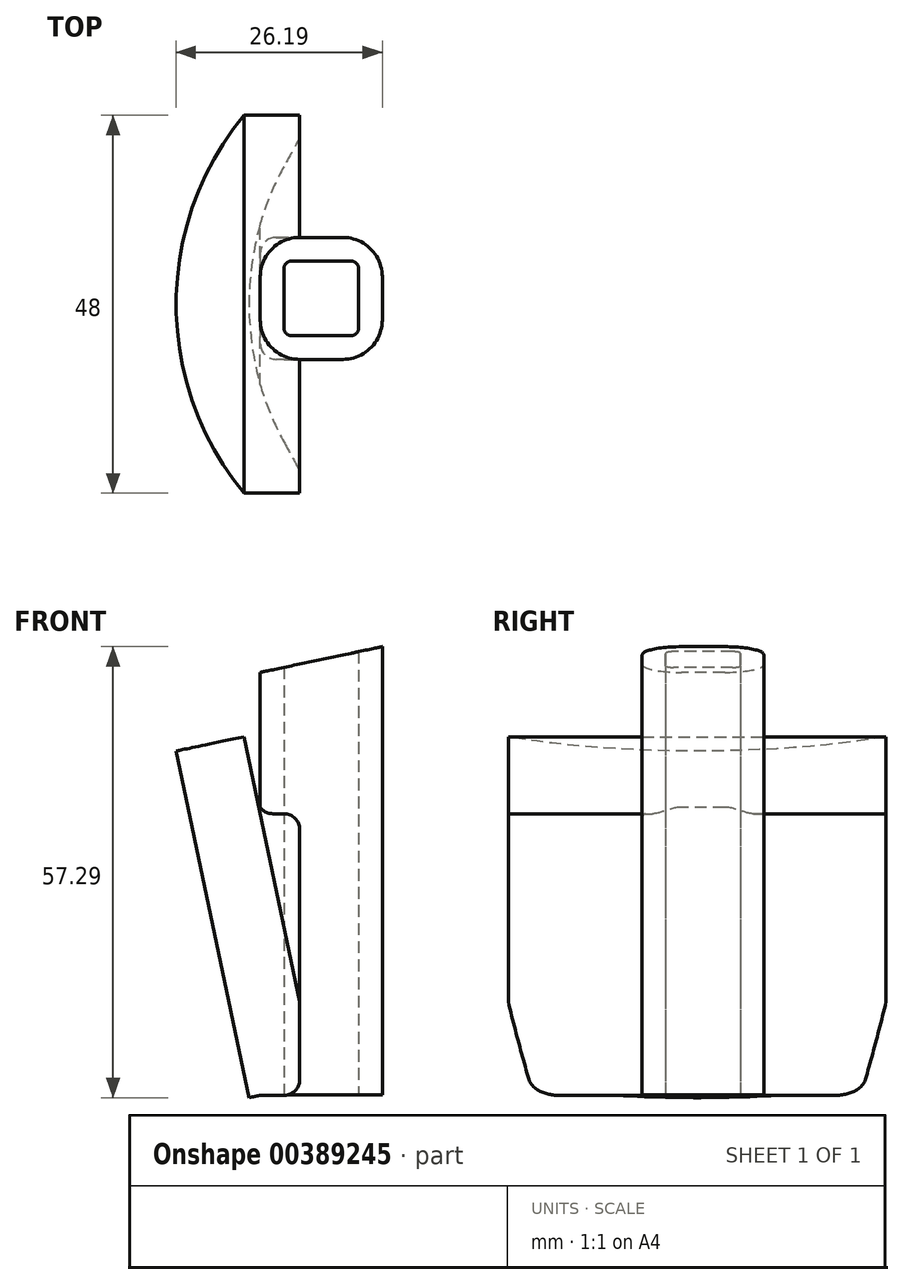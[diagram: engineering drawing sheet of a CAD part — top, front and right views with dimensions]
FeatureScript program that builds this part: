
annotation { "Feature Type Name" : "Feature", "Feature Type Description" : "" }
export const myFeature = defineFeature(function(context is Context, id is Id, definition is map)
    precondition{}
    {
        {
            var Q0;
            Q0=qCreatedBy(makeId("Top.planeOp"),FACE);
            var sketch = newSketch(context, id + "F0", { "sketchPlane" : qUnion([Q0])});
            skLineSegment(sketch, "E0.bottom", {"start": v(0, 0) * mm, "end": v(-9.5, 0) * mm});
            skLineSegment(sketch, "E0.top", {"start": v(0, 9.5) * mm, "end": v(-9.5, 9.5) * mm});
            skLineSegment(sketch, "E0.left", {"start": v(0, 0) * mm, "end": v(0, 9.5) * mm});
            skLineSegment(sketch, "E0.right", {"start": v(-9.5, 0) * mm, "end": v(-9.5, 9.5) * mm});
            skLineSegment(sketch, "E1.0", {"start": v(3, 12.5) * mm, "end": v(-12.5, 12.5) * mm});
            skLineSegment(sketch, "E1.1", {"start": v(3, -3) * mm, "end": v(3, 12.5) * mm});
            skLineSegment(sketch, "E1.2", {"start": v(3, -3) * mm, "end": v(-12.5, -3) * mm});
            skLineSegment(sketch, "E1.3", {"start": v(-12.5, -3) * mm, "end": v(-12.5, 12.5) * mm});
            skSolve(sketch);
        }
        {
            var Q0;
            Q0=makeQuery(id+"F0.imprint","IMPRINT",FACE,{"disambiguationData":[TD([[makeQuery(id+"F0.imprint","IMPRINT",EDGE,{"derivedFrom":sQuery(id+"F0.wireOp",EDGE,"E0.bottom")}),1.0]])]});
            extrude(context, id + "F1", {"entities" : qUnion([Q0]), "depth" : 100 * mm});
        }
        {
            var Q0;
            Q0=makeQuery(id+"F1.opExtrude","SWEPT_EDGE",EDGE,{"disambiguationData":[OSD([sQuery(id+"F0.wireOp",EDGE,"E1.2"),sQuery(id+"F0.wireOp",EDGE,"E1.3")])]});
            var Q1;
            Q1=makeQuery(id+"F1.opExtrude","SWEPT_EDGE",EDGE,{"disambiguationData":[OSD([sQuery(id+"F0.wireOp",EDGE,"E1.0"),sQuery(id+"F0.wireOp",EDGE,"E1.3")])]});
            var Q2;
            Q2=makeQuery(id+"F1.opExtrude","SWEPT_EDGE",EDGE,{"disambiguationData":[OSD([sQuery(id+"F0.wireOp",EDGE,"E1.0"),sQuery(id+"F0.wireOp",EDGE,"E1.1")])]});
            var Q3;
            Q3=makeQuery(id+"F1.opExtrude","SWEPT_EDGE",EDGE,{"disambiguationData":[OSD([sQuery(id+"F0.wireOp",EDGE,"E1.1"),sQuery(id+"F0.wireOp",EDGE,"E1.2")])]});
            fillet(context, id + "F2", {"entities" : qUnion([Q0, Q1, Q2, Q3]), "radius" : 5 * mm, "tangentPropagation" : true, "allowEdgeOverflow" : false});
        }
        {
            var Q0;
            Q0=makeQuery(id+"F1.opExtrude","SWEPT_EDGE",EDGE,{"disambiguationData":[OSD([sQuery(id+"F0.wireOp",EDGE,"E0.top"),sQuery(id+"F0.wireOp",EDGE,"E0.right")])]});
            var Q1;
            Q1=makeQuery(id+"F1.opExtrude","SWEPT_EDGE",EDGE,{"disambiguationData":[OSD([sQuery(id+"F0.wireOp",EDGE,"E0.top"),sQuery(id+"F0.wireOp",EDGE,"E0.left")])]});
            var Q2;
            Q2=makeQuery(id+"F1.opExtrude","SWEPT_EDGE",EDGE,{"disambiguationData":[OSD([sQuery(id+"F0.wireOp",EDGE,"E0.bottom"),sQuery(id+"F0.wireOp",EDGE,"E0.left")])]});
            var Q3;
            Q3=makeQuery(id+"F1.opExtrude","SWEPT_EDGE",EDGE,{"disambiguationData":[OSD([sQuery(id+"F0.wireOp",EDGE,"E0.bottom"),sQuery(id+"F0.wireOp",EDGE,"E0.right")])]});
            fillet(context, id + "F3", {"entities" : qUnion([Q0, Q1, Q2, Q3]), "radius" : 1 * mm, "tangentPropagation" : true, "allowEdgeOverflow" : false});
        }
        {
            var Q0;
            Q0=makeQuery(id+"F0.imprint","IMPRINT",FACE,{"disambiguationData":[TD([[makeQuery(id+"F0.imprint","IMPRINT",EDGE,{"derivedFrom":sQuery(id+"F0.wireOp",EDGE,"E0.bottom")}),-1.0]])]});
            var Q1;
            Q1=makeQuery(id+"F0.imprint","IMPRINT",FACE,{"disambiguationData":[TD([[makeQuery(id+"F0.imprint","IMPRINT",EDGE,{"derivedFrom":sQuery(id+"F0.wireOp",EDGE,"E0.bottom")}),1.0]])]});
            extrude(context, id + "F4", {"entities" : qUnion([Q0, Q1]), "operationType" : NewBodyOperationType.ADD, "depth" : 2 * mm});
        }
        {
            var Q0;
            Q0=makeQuery(id+"F4.opExtrude","SWEPT_EDGE",EDGE,{"disambiguationData":[OSD([sQuery(id+"F0.wireOp",EDGE,"E1.2"),sQuery(id+"F0.wireOp",EDGE,"E1.3")])]});
            var Q1;
            Q1=makeQuery(id+"F4.opExtrude","SWEPT_EDGE",EDGE,{"disambiguationData":[OSD([sQuery(id+"F0.wireOp",EDGE,"E1.1"),sQuery(id+"F0.wireOp",EDGE,"E1.2")])]});
            var Q2;
            Q2=makeQuery(id+"F4.opExtrude","SWEPT_EDGE",EDGE,{"disambiguationData":[OSD([sQuery(id+"F0.wireOp",EDGE,"E1.0"),sQuery(id+"F0.wireOp",EDGE,"E1.1")])]});
            var Q3;
            Q3=makeQuery(id+"F4.opExtrude","SWEPT_EDGE",EDGE,{"disambiguationData":[OSD([sQuery(id+"F0.wireOp",EDGE,"E1.0"),sQuery(id+"F0.wireOp",EDGE,"E1.3")])]});
            fillet(context, id + "F5", {"entities" : qUnion([Q0, Q1, Q2, Q3]), "radius" : 2 * mm, "tangentPropagation" : true, "allowEdgeOverflow" : false});
        }
        {
            var Q0;
            Q0=qCreatedBy(makeId("Front.planeOp"),FACE);
            var sketch = newSketch(context, id + "F6", { "sketchPlane" : qUnion([Q0])});
            skLineSegment(sketch, "E2", {"start": v(-23.85, 87.89) * mm, "end": v(23.32, 97.82) * mm});
            skLineSegment(sketch, "E3.0", {"start": v(-26.94, 102.56) * mm, "end": v(20.23, 112.5) * mm});
            skLineSegment(sketch, "E4", {"start": v(-26.94, 102.56) * mm, "end": v(-23.85, 87.89) * mm});
            skLineSegment(sketch, "E5", {"start": v(20.23, 112.5) * mm, "end": v(23.32, 97.82) * mm});
            skLineSegment(sketch, "E6", {"start": v(-13.99, 36.24) * mm, "end": v(-12.51, 36.55) * mm});
            skLineSegment(sketch, "E7.0", {"start": v(-21.2, 70.49) * mm, "end": v(-12.51, 72.32) * mm});
            skLineSegment(sketch, "E8", {"start": v(-21.2, 70.49) * mm, "end": v(-13.99, 36.24) * mm});
            skLineSegment(sketch, "E9", {"start": v(-12.51, 36.55) * mm, "end": v(-7.49, 36.55) * mm});
            skLineSegment(sketch, "E10", {"start": v(-7.49, 36.55) * mm, "end": v(-7.49, 72.32) * mm});
            skLineSegment(sketch, "E11", {"start": v(-7.49, 72.32) * mm, "end": v(-12.51, 72.32) * mm});
            skSolve(sketch);
        }
        {
            var Q0;
            Q0=makeQuery(id+"F6.imprint","IMPRINT",FACE,{"disambiguationData":[TD([[makeQuery(id+"F6.imprint","IMPRINT",EDGE,{"derivedFrom":sQuery(id+"F6.wireOp",EDGE,"E2")}),1.0]])]});
            extrude(context, id + "F7", {"entities" : qUnion([Q0]), "operationType" : NewBodyOperationType.REMOVE, "oppositeDirection" : true, "depth" : 25 * mm, "symmetric" : true});
        }
        {
            var Q0;
            Q0=makeQuery(id+"F6.imprint","IMPRINT",FACE,{"disambiguationData":[TD([[makeQuery(id+"F6.imprint","IMPRINT",EDGE,{"derivedFrom":sQuery(id+"F6.wireOp",EDGE,"E6")}),1.0]])]});
            extrude(context, id + "F8", {"entities" : qUnion([Q0]), "operationType" : NewBodyOperationType.ADD, "depth" : 20 * mm, "offsetDistance" : 25 * mm});
        }
        {
            var Q0;
            Q0=makeQuery(id+"F8.opExtrude","CAP_FACE",FACE,{"disambiguationData":[OSD([sQuery(id+"F6.wireOp",EDGE,"E6"),sQuery(id+"F6.wireOp",EDGE,"E7.0"),sQuery(id+"F6.wireOp",EDGE,"E8"),sQuery(id+"F6.wireOp",EDGE,"E9"),sQuery(id+"F6.wireOp",EDGE,"E10"),sQuery(id+"F6.wireOp",EDGE,"E11")])],"isStart":false});
            extrude(context, id + "F9", {"entities" : qUnion([Q0]), "operationType" : NewBodyOperationType.ADD, "oppositeDirection" : true, "depth" : 48 * mm, "offsetDistance" : 25 * mm});
        }
        {
            var Q0;
            {var subQ0=sQuery(id+"F0.wireOp",EDGE,"E1.3");var subQ1=sQuery(id+"F0.wireOp",EDGE,"E1.2");var subQ2=sQuery(id+"F0.wireOp",EDGE,"E1.1");var subQ3=sQuery(id+"F0.wireOp",EDGE,"E1.0");Q0=makeQuery(id+"F4.boolean.opBoolean","MERGE",FACE,{"derivedFrom":[makeQuery(id+"F1.opExtrude","CAP_FACE",FACE,{"disambiguationData":[OSD([sQuery(id+"F0.wireOp",EDGE,"E0.bottom"),sQuery(id+"F0.wireOp",EDGE,"E0.top"),sQuery(id+"F0.wireOp",EDGE,"E0.left"),sQuery(id+"F0.wireOp",EDGE,"E0.right"),subQ3,subQ2,subQ1,subQ0])],"isStart":true}),makeQuery(id+"F4.opExtrude","CAP_FACE",FACE,{"disambiguationData":[OSD([subQ3,subQ2,subQ1,subQ0])],"isStart":true})]});}
            extrude(context, id + "F10", {"entities" : qUnion([Q0]), "operationType" : NewBodyOperationType.REMOVE, "oppositeDirection" : true, "depth" : 36.6 * mm, "offsetDistance" : 25 * mm});
        }
        {
            var Q0;
            {var subQ0=sQuery(id+"F6.wireOp",EDGE,"E7.0");Q0=makeQuery(id+"F9.boolean.opBoolean","MERGE",FACE,{"derivedFrom":[makeQuery(id+"F8.opExtrude","SWEPT_FACE",FACE,{"disambiguationData":[OSD([subQ0])]}),makeQuery(id+"F9.opExtrude","SWEPT_FACE",FACE,{"disambiguationData":[OSD([subQ0])]})]});}
            var sketch = newSketch(context, id + "F11", { "sketchPlane" : qUnion([Q0])});
            skArc(sketch, "E12", {"start": v(2.65, 28) * mm, "mid": v(-6.15, 4) * mm, "end": v(2.65, -20) * mm});
            skLineSegment(sketch, "E13", {"start": v(2.65, -20) * mm, "end": v(-6.22, -20) * mm});
            skLineSegment(sketch, "E14", {"start": v(-6.22, -20) * mm, "end": v(-6.22, 28) * mm});
            skLineSegment(sketch, "E15", {"start": v(-6.22, 28) * mm, "end": v(2.65, 28) * mm});
            skSolve(sketch);
        }
        {
            var Q0;
            Q0=makeQuery(id+"F11.imprint","IMPRINT",FACE,{"disambiguationData":[TD([[makeQuery(id+"F11.imprint","IMPRINT",EDGE,{"derivedFrom":sQuery(id+"F11.wireOp",EDGE,"E12")}),-1.0]])]});
            extrude(context, id + "F12", {"entities" : qUnion([Q0]), "operationType" : NewBodyOperationType.REMOVE, "endBound" : BoundingType.THROUGH_ALL, "oppositeDirection" : true, "depth" : 25 * mm, "offsetDistance" : 25 * mm});
        }
        {
            var Q0;
            {var subQ0=sQuery(id+"F6.wireOp",EDGE,"E7.0");Q0=makeQuery(id+"F9.boolean.opBoolean","MERGE",FACE,{"derivedFrom":[makeQuery(id+"F8.opExtrude","SWEPT_FACE",FACE,{"disambiguationData":[OSD([subQ0])]}),makeQuery(id+"F9.opExtrude","SWEPT_FACE",FACE,{"disambiguationData":[OSD([subQ0])]})]});}
            extrude(context, id + "F13", {"entities" : qUnion([Q0]), "operationType" : NewBodyOperationType.ADD, "depth" : 10 * mm, "offsetDistance" : 25 * mm});
        }
        {
            var Q0;
            {var subQ0=sQuery(id+"F6.wireOp",EDGE,"E11");var subQ1=sQuery(id+"F6.wireOp",EDGE,"E7.0");Q0=makeQuery(id+"F13.boolean.opBoolean","MERGE",EDGE,{"derivedFrom":[makeQuery(id+"F9.boolean.opBoolean","MERGE",EDGE,{"derivedFrom":[makeQuery(id+"F8.opExtrude","SWEPT_EDGE",EDGE,{"disambiguationData":[OSD([subQ1,subQ0])]}),makeQuery(id+"F9.opExtrude","SWEPT_EDGE",EDGE,{"disambiguationData":[OSD([subQ1,subQ0])]})]}),makeQuery(id+"F13.opExtrude","CAP_EDGE",EDGE,{"disambiguationData":[OSD([subQ1,subQ0])],"isStart":true})]});}
            var Q1;
            Q1=makeQuery(id+"F8.opExtrude","SWEPT_EDGE",EDGE,{"disambiguationData":[OSD([sQuery(id+"F6.wireOp",EDGE,"E10"),sQuery(id+"F6.wireOp",EDGE,"E11")])]});
            var Q2;
            {var subQ0=sQuery(id+"F6.wireOp",EDGE,"E11");var subQ1=sQuery(id+"F6.wireOp",EDGE,"E10");Q2=makeQuery(id+"F9.boolean.opBoolean","SPLIT",EDGE,{"disambiguationData":[topologyDisambiguationEdgeConnected([makeQuery(id+"F8.opExtrude","SWEPT_FACE",FACE,{"disambiguationData":[OSD([subQ0])]}),makeQuery(id+"F9.opExtrude","SWEPT_FACE",FACE,{"disambiguationData":[OSD([subQ1])]}),makeQuery(id+"F9.opExtrude","SWEPT_FACE",FACE,{"disambiguationData":[OSD([subQ0])]})])],"derivedFrom":makeQuery(id+"F9.opExtrude","SWEPT_EDGE",EDGE,{"disambiguationData":[OSD([subQ1,subQ0])]})});}
            fillet(context, id + "F14", {"entities" : qUnion([Q0, Q1, Q2]), "radius" : 2 * mm, "tangentPropagation" : true, "allowEdgeOverflow" : false});
        }
        {
            var Q0;
            {var subQ0=sQuery(id+"F6.wireOp",EDGE,"E9");var subQ1=sQuery(id+"F6.wireOp",EDGE,"E10");Q0=makeQuery(id+"F9.boolean.opBoolean","SPLIT",EDGE,{"disambiguationData":[topologyDisambiguationEdgeConnected([makeQuery(id+"F8.opExtrude","SWEPT_FACE",FACE,{"disambiguationData":[OSD([subQ0])]}),makeQuery(id+"F9.opExtrude","SWEPT_FACE",FACE,{"disambiguationData":[OSD([subQ0])]}),makeQuery(id+"F9.opExtrude","SWEPT_FACE",FACE,{"disambiguationData":[OSD([subQ1])]})])],"derivedFrom":makeQuery(id+"F9.opExtrude","SWEPT_EDGE",EDGE,{"disambiguationData":[OSD([subQ0,subQ1])]})});}
            var Q1;
            Q1=makeQuery(id+"F8.opExtrude","SWEPT_EDGE",EDGE,{"disambiguationData":[OSD([sQuery(id+"F6.wireOp",EDGE,"E9"),sQuery(id+"F6.wireOp",EDGE,"E10")])]});
            fillet(context, id + "F15", {"entities" : qUnion([Q0, Q1]), "radius" : 2 * mm, "tangentPropagation" : true, "allowEdgeOverflow" : false});
        }
        {
            var Q0;
            Q0=makeQuery(id+"F9.boolean.opBoolean","SPLIT",FACE,{"derivedFrom":makeQuery(id+"F9.opExtrude","SWEPT_FACE",FACE,{"disambiguationData":[OSD([sQuery(id+"F6.wireOp",EDGE,"E11")])]})});
            extrude(context, id + "F16", {"entities" : qUnion([Q0]), "operationType" : NewBodyOperationType.REMOVE, "endBound" : BoundingType.THROUGH_ALL, "oppositeDirection" : true, "depth" : 25 * mm, "offsetDistance" : 25 * mm});
        }
    });
